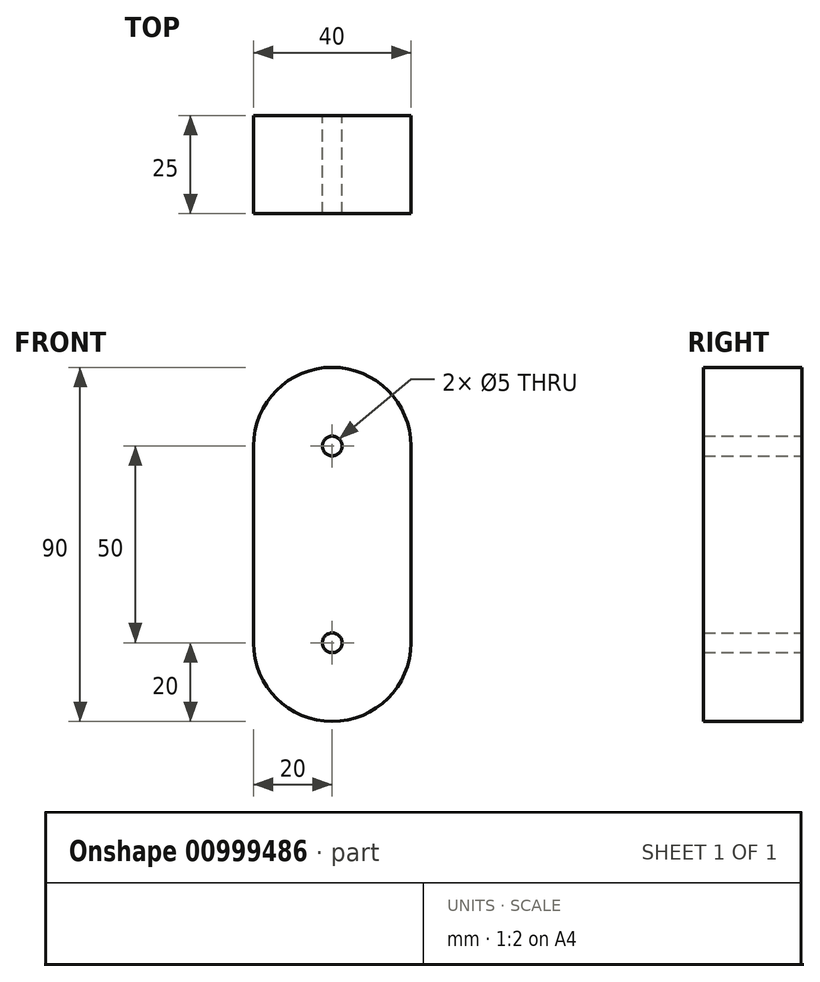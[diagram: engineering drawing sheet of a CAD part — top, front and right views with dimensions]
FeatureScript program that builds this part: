
annotation { "Feature Type Name" : "Feature", "Feature Type Description" : "" }
export const myFeature = defineFeature(function(context is Context, id is Id, definition is map)
    precondition{}
    {
        {
            var Q0;
            Q0=qCreatedBy(makeId("Front.planeOp"),FACE);
            var sketch = newSketch(context, id + "F0", { "sketchPlane" : qUnion([Q0])});
            skArc(sketch, "E0", {"start": v(-20, 0) * mm, "mid": v(0, -20) * mm, "end": v(20, 0) * mm});
            skLineSegment(sketch, "E1", {"start": v(20, 0) * mm, "end": v(20, 50) * mm});
            skLineSegment(sketch, "E2", {"start": v(-20, 0) * mm, "end": v(-20, 50) * mm});
            skLineSegment(sketch, "E3", {"start": v(-20, 50) * mm, "end": v(20, 50) * mm});
            skArc(sketch, "E4", {"start": v(20, 50) * mm, "mid": v(0, 70) * mm, "end": v(-20, 50) * mm});
            skCircle(sketch, "E5", {"center": v(0, 50) * mm, "radius": 2.5 * mm});
            skCircle(sketch, "E6", {"center": v(0, 0) * mm, "radius": 2.5 * mm});
            skSolve(sketch);
        }
        {
            var Q0;
            Q0=makeQuery(id+"F0.imprint","IMPRINT",FACE,{"disambiguationData":[TD([[makeQuery(id+"F0.imprint","IMPRINT",EDGE,{"derivedFrom":sQuery(id+"F0.wireOp",EDGE,"E0")}),1.0]])]});
            var Q1;
            {var subQ0=sQuery(id+"F0.wireOp",EDGE,"E4");Q1=makeQuery(id+"F0.imprint","IMPRINT",FACE,{"disambiguationData":[TD([[makeQuery(id+"F0.imprint","IMPRINT",EDGE,{"derivedFrom":subQ0}),1.0]])]});}
            extrude(context, id + "F1", {"entities" : qUnion([Q0, Q1]), "depth" : 25 * mm, "offsetDistance" : 25 * mm});
        }
    });
